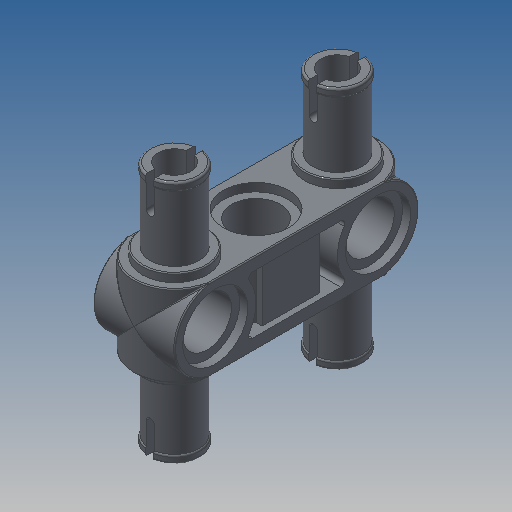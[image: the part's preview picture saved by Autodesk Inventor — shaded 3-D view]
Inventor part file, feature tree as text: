
AUTODESK INVENTOR PART (.ipt)
format: ipt  version: 2022.2 (Build 262287000, 287)  size: 596,992 bytes
history: native  units: in
note: dims shown in document units (in); Inventor stores cm internally (conversion verified against a paired STEP export)
features: extrude x7, sketch x6, mirror x3, fillet x2, revolve x1
ambient origin geometry x8: Origin, YZ Plane, XZ Plane, XY Plane, X Axis, Y Axis, Z Axis, Center Point
bodies: Solid1 (feature_tree)
feature tree (19):
  sketch  "Sketch2"  dims[d0=0.6299in d1=0.315in]
  extrude  "Extrusion1"  Depth=0.315in
  sketch  "Sketch3"  dims[d2=0.189in d4=0.0461in]
  extrude  "Extrusion2"  Depth=0.0461in
  extrude  "Extrusion3"  Depth=0.315in
  extrude  "Extrusion4"  Depth=0.189in
  revolve  "Revolution1"  [1 undecoded]
  extrude  "Extrusion5"  Depth=0.315in
  extrude  "Extrusion7"  TaperAngle=0.0deg  [1 undecoded]
  mirror  "Mirror1"
  mirror  "Mirror2"
  extrude  "Extrusion6"  Depth=0.315in
  mirror  "Mirror3"
  fillet  "Fillet1"  [1 undecoded]
  fillet  "Fillet2"  Radius=0.315in
  sketch  "Sketch4"  dims[d5=0.0461in d6=0.315in]
  sketch  "Sketch5"  dims[d7=0.0in d8=0.189in]
  sketch  "Sketch6"  dims[d9=0.315in d10=0.022in]
  sketch  "Sketch7"  dims[d11=0.2227in d12=0.315in d13=0.0in d14=0.315in d15=0.0in d16=0.315in d17=0.0in d18=0.126in d19=0.189in d20=0.1969in d21=0.315in d22=0.252in d23=0.0315in d24=90.0deg d25=0.1339in d26=0.0315in d27=0.315in d28=0.0in d29=0.252in d30=0.0315in d31=0.0in d32=0.252in d33=0.0315in d34=0.0in d35=0.0039in d36=0.0039in d37=0.0157in d38=0.0079in]
note: 3 required parameter values undecoded (feature->parameter linkage not recoverable at this tier; creation-order binding heuristic only, values carry confidence <= 0.55)